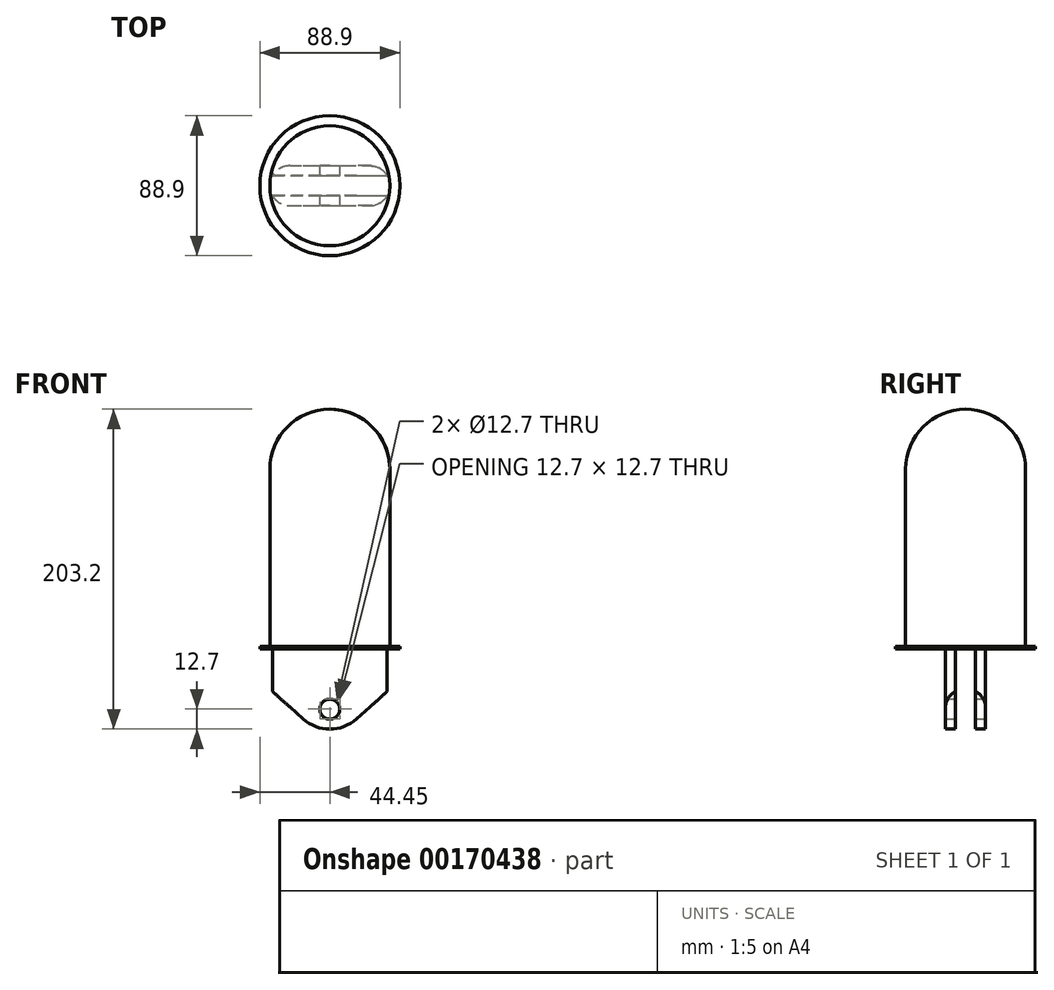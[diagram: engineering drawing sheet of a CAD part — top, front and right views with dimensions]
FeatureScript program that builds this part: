
annotation { "Feature Type Name" : "Feature", "Feature Type Description" : "" }
export const myFeature = defineFeature(function(context is Context, id is Id, definition is map)
    precondition{}
    {
        {
            var Q0;
            Q0=qCreatedBy(makeId("Top.planeOp"),FACE);
            var sketch = newSketch(context, id + "F0", { "sketchPlane" : qUnion([Q0])});
            skCircle(sketch, "E0", {"center": v(0, 0) * mm, "radius": 38.1 * mm});
            skCircle(sketch, "E1", {"center": v(0, 0) * mm, "radius": 44.45 * mm});
            skSolve(sketch);
        }
        {
            var Q0;
            Q0=makeQuery(id+"F0.imprint","IMPRINT",FACE,{"disambiguationData":[TD([[makeQuery(id+"F0.imprint","IMPRINT",EDGE,{"derivedFrom":sQuery(id+"F0.wireOp",EDGE,"E0")}),1.0]])]});
            extrude(context, id + "F1", {"entities" : qUnion([Q0]), "depth" : 152.4 * mm});
        }
        {
            var Q0;
            Q0=makeQuery(id+"F1.opExtrude","CAP_EDGE",EDGE,{"disambiguationData":[OSD([sQuery(id+"F0.wireOp",EDGE,"E0")])],"isStart":false});
            fillet(context, id + "F2", {"entities" : qUnion([Q0]), "radius" : 38.1 * mm, "tangentPropagation" : true, "allowEdgeOverflow" : false});
        }
        {
            var Q0;
            Q0=qCreatedBy(makeId("Front.planeOp"),FACE);
            var sketch = newSketch(context, id + "F3", { "sketchPlane" : qUnion([Q0])});
            skLineSegment(sketch, "E2.left", {"start": v(38.1, -25.4) * mm, "end": v(38.1, 0) * mm});
            skLineSegment(sketch, "E2.right", {"start": v(-38.1, -25.4) * mm, "end": v(-38.1, 0) * mm});
            skPoint(sketch, "E2.middle", {"position": v(0, 0) * mm});
            skArc(sketch, "E3", {"start": v(-16.93, -44.33) * mm, "mid": v(0, -50.8) * mm, "end": v(16.93, -44.33) * mm});
            skLineSegment(sketch, "E4", {"start": v(-38.1, -25.4) * mm, "end": v(-16.93, -44.33) * mm});
            skLineSegment(sketch, "E5", {"start": v(38.1, -25.4) * mm, "end": v(16.93, -44.33) * mm});
            skLineSegment(sketch, "E6", {"start": v(-38.1, 0) * mm, "end": v(38.1, 0) * mm});
            skLineSegment(sketch, "E7", {"start": v(0, 0) * mm, "end": v(0, -38.1) * mm});
            skCircle(sketch, "E8", {"center": v(0, -38.1) * mm, "radius": 6.35 * mm});
            skSolve(sketch);
        }
        {
            var Q0;
            {var subQ1=sQuery(id+"F3.wireOp",EDGE,"E2.left");Q0=makeQuery(id+"F3.imprint","IMPRINT",FACE,{"disambiguationData":[TD([[makeQuery(id+"F3.imprint","IMPRINT",EDGE,{"derivedFrom":subQ1}),1.0]])]});}
            extrude(context, id + "F4", {"entities" : qUnion([Q0]), "operationType" : NewBodyOperationType.ADD, "endBound" : BoundingType.SYMMETRIC, "depth" : 25.4 * mm});
        }
        {
            var Q0;
            Q0=makeQuery(id+"F4.opExtrude","CAP_EDGE",EDGE,{"disambiguationData":[OSD([sQuery(id+"F3.wireOp",EDGE,"E2.left")])],"isStart":false});
            var Q1;
            Q1=makeQuery(id+"F4.opExtrude","CAP_EDGE",EDGE,{"disambiguationData":[OSD([sQuery(id+"F3.wireOp",EDGE,"E2.left")])],"isStart":true});
            var Q2;
            Q2=makeQuery(id+"F4.opExtrude","CAP_EDGE",EDGE,{"disambiguationData":[OSD([sQuery(id+"F3.wireOp",EDGE,"E2.right")])],"isStart":true});
            var Q3;
            Q3=makeQuery(id+"F4.opExtrude","CAP_EDGE",EDGE,{"disambiguationData":[OSD([sQuery(id+"F3.wireOp",EDGE,"E2.right")])],"isStart":false});
            fillet(context, id + "F5", {"entities" : qUnion([Q0, Q1, Q2, Q3]), "radius" : 12.7 * mm, "tangentPropagation" : true, "allowEdgeOverflow" : false});
        }
        {
            var Q0;
            Q0=qCreatedBy(makeId("Right.planeOp"),FACE);
            var sketch = newSketch(context, id + "F6", { "sketchPlane" : qUnion([Q0])});
            skLineSegment(sketch, "E9.bottom", {"start": v(6.35, -50.8) * mm, "end": v(-6.35, -50.8) * mm});
            skLineSegment(sketch, "E9.left", {"start": v(6.35, -50.8) * mm, "end": v(6.35, 0) * mm});
            skLineSegment(sketch, "E9.right", {"start": v(-6.35, -50.8) * mm, "end": v(-6.35, 0) * mm});
            skPoint(sketch, "E9.middle", {"position": v(0, 0) * mm});
            skLineSegment(sketch, "E10", {"start": v(-6.35, 0) * mm, "end": v(6.35, 0) * mm});
            skSolve(sketch);
        }
        {
            var Q0;
            Q0 = qSketchRegion(id + "F6", true);
            extrude(context, id + "F7", {"entities" : qUnion([Q0]), "operationType" : NewBodyOperationType.REMOVE, "endBound" : BoundingType.SYMMETRIC, "oppositeDirection" : true, "depth" : 76.2 * mm});
        }
        {
            var Q0;
            Q0=makeQuery(id+"F0.imprint","IMPRINT",FACE,{"disambiguationData":[TD([[makeQuery(id+"F0.imprint","IMPRINT",EDGE,{"derivedFrom":sQuery(id+"F0.wireOp",EDGE,"E0")}),-1.0]])]});
            extrude(context, id + "F8", {"entities" : qUnion([Q0]), "operationType" : NewBodyOperationType.ADD, "depth" : 1.59 * mm});
        }
    });
